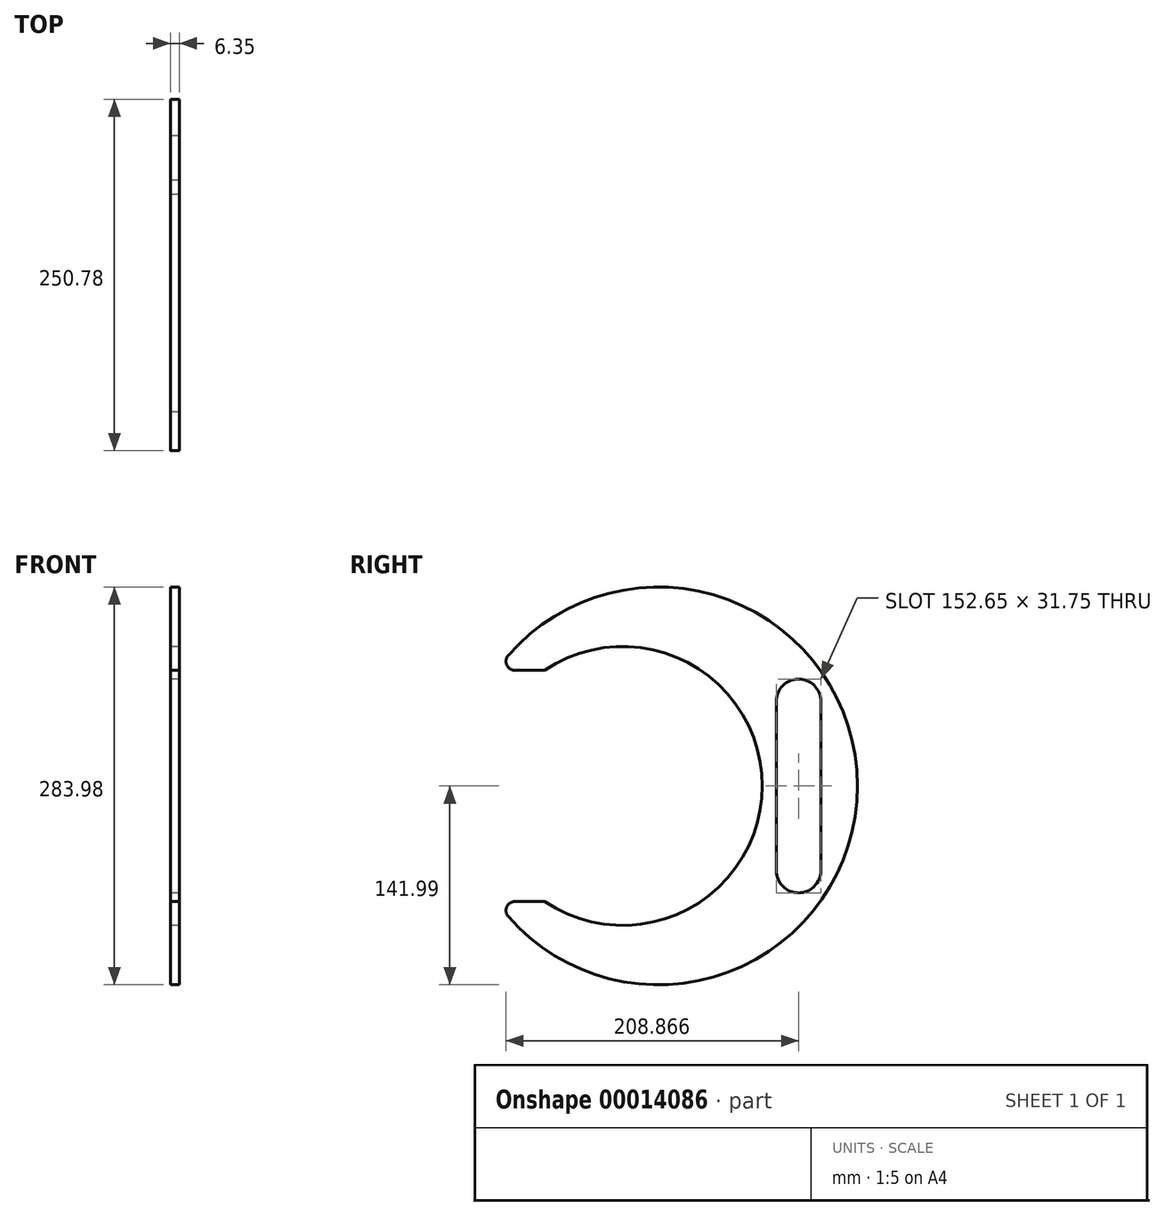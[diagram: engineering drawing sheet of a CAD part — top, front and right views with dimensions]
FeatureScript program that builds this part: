
annotation { "Feature Type Name" : "Feature", "Feature Type Description" : "" }
export const myFeature = defineFeature(function(context is Context, id is Id, definition is map)
    precondition{}
    {
        {
            var Q0;
            Q0=qCreatedBy(makeId("Right.planeOp"),FACE);
            var sketch = newSketch(context, id + "F0", { "sketchPlane" : qUnion([Q0])});
            skArc(sketch, "E0", {"start": v(-55.67, -82.55) * mm, "mid": v(99.57, 0) * mm, "end": v(-55.67, 82.55) * mm});
            skLineSegment(sketch, "E1", {"start": v(0, 74.3) * mm, "end": v(0, -77.22) * mm, "construction": true});
            skLineSegment(sketch, "E2.0", {"start": v(25.4, 74.3) * mm, "end": v(25.4, -77.22) * mm, "construction": true});
            skLineSegment(sketch, "E3", {"start": v(-80.3, 0) * mm, "end": v(95.23, 0) * mm, "construction": true});
            skArc(sketch, "E4", {"start": v(-81.84, -93.06) * mm, "mid": v(167.39, 0) * mm, "end": v(-81.84, 93.06) * mm});
            skLineSegment(sketch, "E5.0", {"start": v(-77.04, 82.55) * mm, "end": v(-55.67, 82.55) * mm});
            skLineSegment(sketch, "E6.0.MirrorCS", {"start": v(-77.04, -82.55) * mm, "end": v(-55.67, -82.55) * mm});
            skPoint(sketch, "E7.orphan", {"position": v(95.23, 82.55) * mm});
            skPoint(sketch, "E8.trimOffspring.end.orphan", {"position": v(95.23, -82.55) * mm});
            skPoint(sketch, "E9.orphan", {"position": v(-80.3, 82.55) * mm});
            skPoint(sketch, "E10.orphan", {"position": v(-80.3, -82.55) * mm});
            skPoint(sketch, "E11.visualSharp", {"position": v(-90.12, 82.55) * mm});
            skArc(sketch, "E11.filletArc", {"start": v(-81.84, 93.06) * mm, "mid": v(-82.82, 86.26) * mm, "end": v(-77.04, 82.55) * mm});
            skPoint(sketch, "E12.visualSharp", {"position": v(-90.12, -82.55) * mm});
            skArc(sketch, "E12.filletArc", {"start": v(-77.04, -82.55) * mm, "mid": v(-82.82, -86.26) * mm, "end": v(-81.84, -93.06) * mm});
            skLineSegment(sketch, "E13.0", {"start": v(125.48, 74.3) * mm, "end": v(125.48, -77.22) * mm, "construction": true});
            skLineSegment(sketch, "E14.0", {"start": v(-80.3, -60.45) * mm, "end": v(125.48, -60.45) * mm, "construction": true});
            skArc(sketch, "E15", {"start": v(109.6, -60.45) * mm, "mid": v(125.48, -76.33) * mm, "end": v(141.35, -60.45) * mm});
            skArc(sketch, "E16.0.MirrorC", {"start": v(109.6, 60.45) * mm, "mid": v(125.48, 76.33) * mm, "end": v(141.35, 60.45) * mm});
            skLineSegment(sketch, "E17", {"start": v(109.6, 60.45) * mm, "end": v(109.6, -60.45) * mm});
            skLineSegment(sketch, "E18.0.MirrorCS", {"start": v(141.35, 60.45) * mm, "end": v(141.35, -60.45) * mm});
            skSolve(sketch);
        }
        {
            var Q0;
            Q0 = qSketchRegion(id + "F0", true);
            extrude(context, id + "F1", {"entities" : qUnion([Q0]), "depth" : 6.35 * mm});
        }
    });
